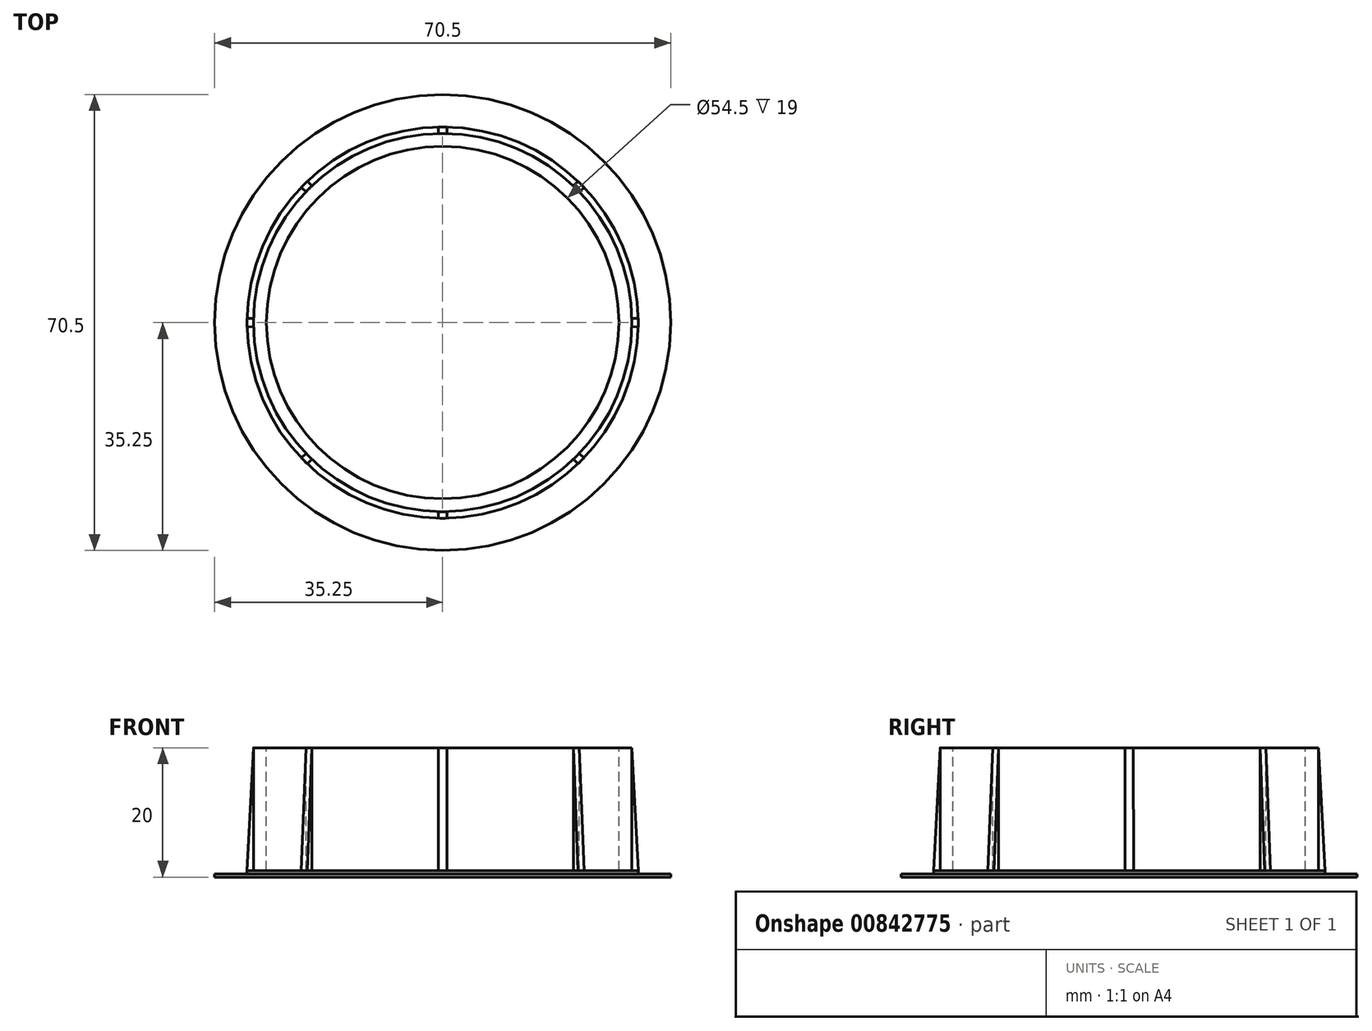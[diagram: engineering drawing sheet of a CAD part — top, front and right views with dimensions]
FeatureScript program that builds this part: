
annotation { "Feature Type Name" : "Feature", "Feature Type Description" : "" }
export const myFeature = defineFeature(function(context is Context, id is Id, definition is map)
    precondition{}
    {
        {
            var Q0;
            Q0=qCreatedBy(makeId("Front.planeOp"),FACE);
            var sketch = newSketch(context, id + "F0", { "sketchPlane" : qUnion([Q0])});
            skLineSegment(sketch, "E0", {"start": v(-30.25, 1) * mm, "end": v(-29.25, 1) * mm});
            skLineSegment(sketch, "E1", {"start": v(-29.25, 1) * mm, "end": v(-29.25, 20) * mm});
            skLineSegment(sketch, "E2", {"start": v(-29.25, 20) * mm, "end": v(-27.25, 20) * mm});
            skLineSegment(sketch, "E3", {"start": v(-27.25, 20) * mm, "end": v(-27.25, 1) * mm});
            skLineSegment(sketch, "E4", {"start": v(-27.25, 1) * mm, "end": v(0, 1) * mm});
            skLineSegment(sketch, "E5", {"start": v(0, 1) * mm, "end": v(0, 0) * mm});
            skLineSegment(sketch, "E6", {"start": v(-30.25, 1) * mm, "end": v(-29.25, 20) * mm});
            skLineSegment(sketch, "E7", {"start": v(0, 0.5) * mm, "end": v(-30.25, 0.5) * mm});
            skLineSegment(sketch, "E8", {"start": v(-30.25, 0.5) * mm, "end": v(-30.25, 1) * mm});
            skLineSegment(sketch, "E9", {"start": v(0, 0) * mm, "end": v(-35.25, 0) * mm});
            skLineSegment(sketch, "E10", {"start": v(-35.25, 0) * mm, "end": v(-35.25, 0.5) * mm});
            skLineSegment(sketch, "E11", {"start": v(-35.25, 0.5) * mm, "end": v(-30.25, 0.5) * mm});
            skSolve(sketch);
        }
        {
            var Q0;
            Q0=makeQuery(id+"F0.imprint","IMPRINT",FACE,{"disambiguationData":[TD([[makeQuery(id+"F0.imprint","IMPRINT",EDGE,{"derivedFrom":sQuery(id+"F0.wireOp",EDGE,"eXFrBWmc-IFv0-ld64-PjX3-9kD5yiLC1V9S")}),-1.0]])]});
            var Q1;
            {var subQ1=sQuery(id+"F0.wireOp",EDGE,"E7");Q1=makeQuery(id+"F0.imprint","IMPRINT",FACE,{"disambiguationData":[TD([[makeQuery(id+"F0.imprint","IMPRINT",EDGE,{"derivedFrom":subQ1}),1.0]])]});}
            var Q2;
            Q2=makeQuery(id+"F0.imprint","IMPRINT",FACE,{"disambiguationData":[TD([[makeQuery(id+"F0.imprint","IMPRINT",EDGE,{"derivedFrom":sQuery(id+"F0.wireOp",EDGE,"E0")}),-1.0]])]});
            var Q3;
            Q3=sQuery(id+"F0.wireOp",EDGE,"E5");
            revolve(context, id + "F1", {"surfaceOperationType" : NewSurfaceOperationType.NEW, "entities" : qUnion([Q0, Q1, Q2]), "axis" : qUnion([Q3]), "revolveType" : RevolveType.FULL});
        }
        {
            var Q0;
            Q0=makeQuery(id+"F0.imprint","IMPRINT",FACE,{"disambiguationData":[TD([[makeQuery(id+"F0.imprint","IMPRINT",EDGE,{"derivedFrom":sQuery(id+"F0.wireOp",EDGE,"E0")}),1.0]])]});
            var Q1;
            Q1=sQuery(id+"F0.wireOp",EDGE,"E5");
            revolve(context, id + "F2", {"surfaceOperationType" : NewSurfaceOperationType.NEW, "entities" : qUnion([Q0]), "axis" : qUnion([Q1]), "revolveType" : RevolveType.SYMMETRIC, "angle" : 2.5 * degree});
        }
        {
            var Q0;
            Q0=makeQuery(id+"F2.opRevolve","SWEPT_BODY",BODY,{"disambiguationData":[OSD([sQuery(id+"F0.wireOp",EDGE,"E0"),sQuery(id+"F0.wireOp",EDGE,"E1"),sQuery(id+"F0.wireOp",EDGE,"E6")])]});
            var Q1;
            Q1=sQuery(id+"F0.wireOp",EDGE,"E5");
            circularPattern(context, id + "F3", {"entities" : qUnion([Q0]), "axis" : qUnion([Q1]), "angle" : 360 * degree, "instanceCount" : 8, "equalSpace" : true});
        }
    });
